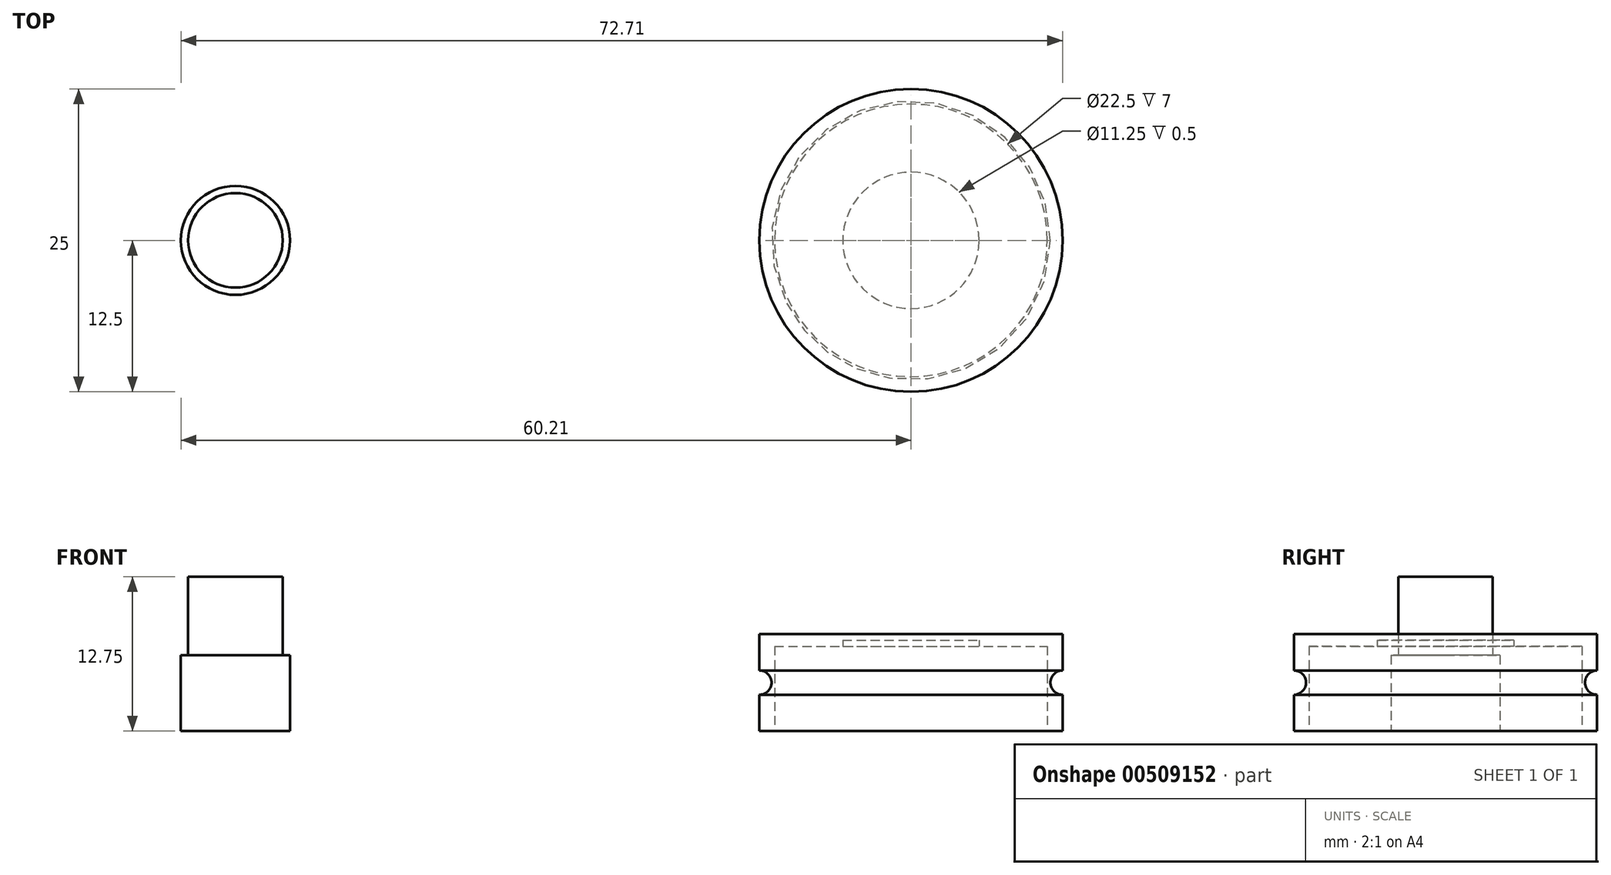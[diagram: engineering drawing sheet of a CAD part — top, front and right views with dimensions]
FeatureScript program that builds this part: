
annotation { "Feature Type Name" : "Feature", "Feature Type Description" : "" }
export const myFeature = defineFeature(function(context is Context, id is Id, definition is map)
    precondition{}
    {
        {
            var Q0;
            Q0=qCreatedBy(makeId("Top.planeOp"),FACE);
            var sketch = newSketch(context, id + "F0", { "sketchPlane" : qUnion([Q0])});
            skCircle(sketch, "E0", {"center": v(0, 0) * mm, "radius": 12.5 * mm});
            skSolve(sketch);
        }
        {
            var Q0;
            Q0=qSketchRegion(id+"F0",true);
            extrude(context, id + "F1", {"entities" : qUnion([Q0]), "depth" : 8 * mm, "offsetDistance" : 25 * mm});
        }
        {
            var Q0;
            Q0=qCreatedBy(makeId("Front.planeOp"),FACE);
            var sketch = newSketch(context, id + "F2", { "sketchPlane" : qUnion([Q0])});
            skCircle(sketch, "E1", {"center": v(-12.5, 4) * mm, "radius": 1 * mm});
            skSolve(sketch);
        }
        {
            var Q0;
            Q0=qSketchRegion(id+"F2",true);
            var Q1;
            Q1=makeQuery(id+"F1.opExtrude","CAP_EDGE",EDGE,{"disambiguationData":[OSD([sQuery(id+"F0.wireOp",EDGE,"E0")])],"isStart":true});
            sweep(context, id + "F3", {"operationType" : NewBodyOperationType.REMOVE, "profiles" : qUnion([Q0]), "path" : qUnion([Q1])});
        }
        {
            var Q0;
            Q0=makeQuery(id+"F1.opExtrude","CAP_FACE",FACE,{"disambiguationData":[OSD([sQuery(id+"F0.wireOp",EDGE,"E0"),sQuery(id+"F0.wireOp",EDGE,"nnjjs8v5-ciEF-tbuS-nztJ-yywfd1xPWN0F")])],"isStart":true});
            var sketch = newSketch(context, id + "F4", { "sketchPlane" : qUnion([Q0])});
            skCircle(sketch, "E2", {"center": v(0, 0) * mm, "radius": 11.25 * mm});
            skSolve(sketch);
        }
        {
            var Q0;
            Q0=makeQuery(id+"F4.imprint","IMPRINT",FACE,{"disambiguationData":[TD([[makeQuery(id+"F4.imprint","IMPRINT",EDGE,{"derivedFrom":sQuery(id+"F4.wireOp",EDGE,"E2")}),1.0]])]});
            extrude(context, id + "F5", {"entities" : qUnion([Q0]), "operationType" : NewBodyOperationType.REMOVE, "oppositeDirection" : true, "depth" : 7 * mm, "offsetDistance" : 25 * mm});
        }
        {
            var Q0;
            Q0=makeQuery(id+"F5.boolean.opBoolean","COPY",FACE,{"derivedFrom":makeQuery(id+"F5.opExtrude","CAP_FACE",FACE,{"disambiguationData":[OSD([sQuery(id+"F4.wireOp",EDGE,"E2")])],"isStart":false})});
            var sketch = newSketch(context, id + "F6", { "sketchPlane" : qUnion([Q0])});
            skCircle(sketch, "E3", {"center": v(0, 0) * mm, "radius": 5.62 * mm});
            skSolve(sketch);
        }
        {
            var Q0;
            Q0 = qSketchRegion(id + "F6", true);
            extrude(context, id + "F7", {"entities" : qUnion([Q0]), "operationType" : NewBodyOperationType.REMOVE, "oppositeDirection" : true, "depth" : 0.5 * mm, "offsetDistance" : 25 * mm});
        }
        {
            var Q0;
            Q0=qCreatedBy(makeId("Top.planeOp"),FACE);
            var sketch = newSketch(context, id + "F8", { "sketchPlane" : qUnion([Q0])});
            skCircle(sketch, "E4", {"center": v(-55.71, 0) * mm, "radius": 4.5 * mm});
            skSolve(sketch);
        }
        {
            var Q0;
            Q0=makeQuery(id+"F8.imprint","IMPRINT",FACE,{"disambiguationData":[TD([[makeQuery(id+"F8.imprint","IMPRINT",EDGE,{"derivedFrom":sQuery(id+"F8.wireOp",EDGE,"E4")}),1.0]])]});
            extrude(context, id + "F9", {"entities" : qUnion([Q0]), "depth" : 6.25 * mm, "offsetDistance" : 25 * mm});
        }
        {
            var Q0;
            Q0=makeQuery(id+"F9.opExtrude","CAP_FACE",FACE,{"disambiguationData":[OSD([sQuery(id+"F8.wireOp",EDGE,"E4")])],"isStart":false});
            var sketch = newSketch(context, id + "F10", { "sketchPlane" : qUnion([Q0])});
            skCircle(sketch, "E5", {"center": v(-55.71, 0) * mm, "radius": 3.9 * mm});
            skSolve(sketch);
        }
        {
            var Q0;
            Q0 = qSketchRegion(id + "F10", true);
            extrude(context, id + "F11", {"entities" : qUnion([Q0]), "operationType" : NewBodyOperationType.ADD, "depth" : 6.5 * mm, "offsetDistance" : 25 * mm});
        }
    });
